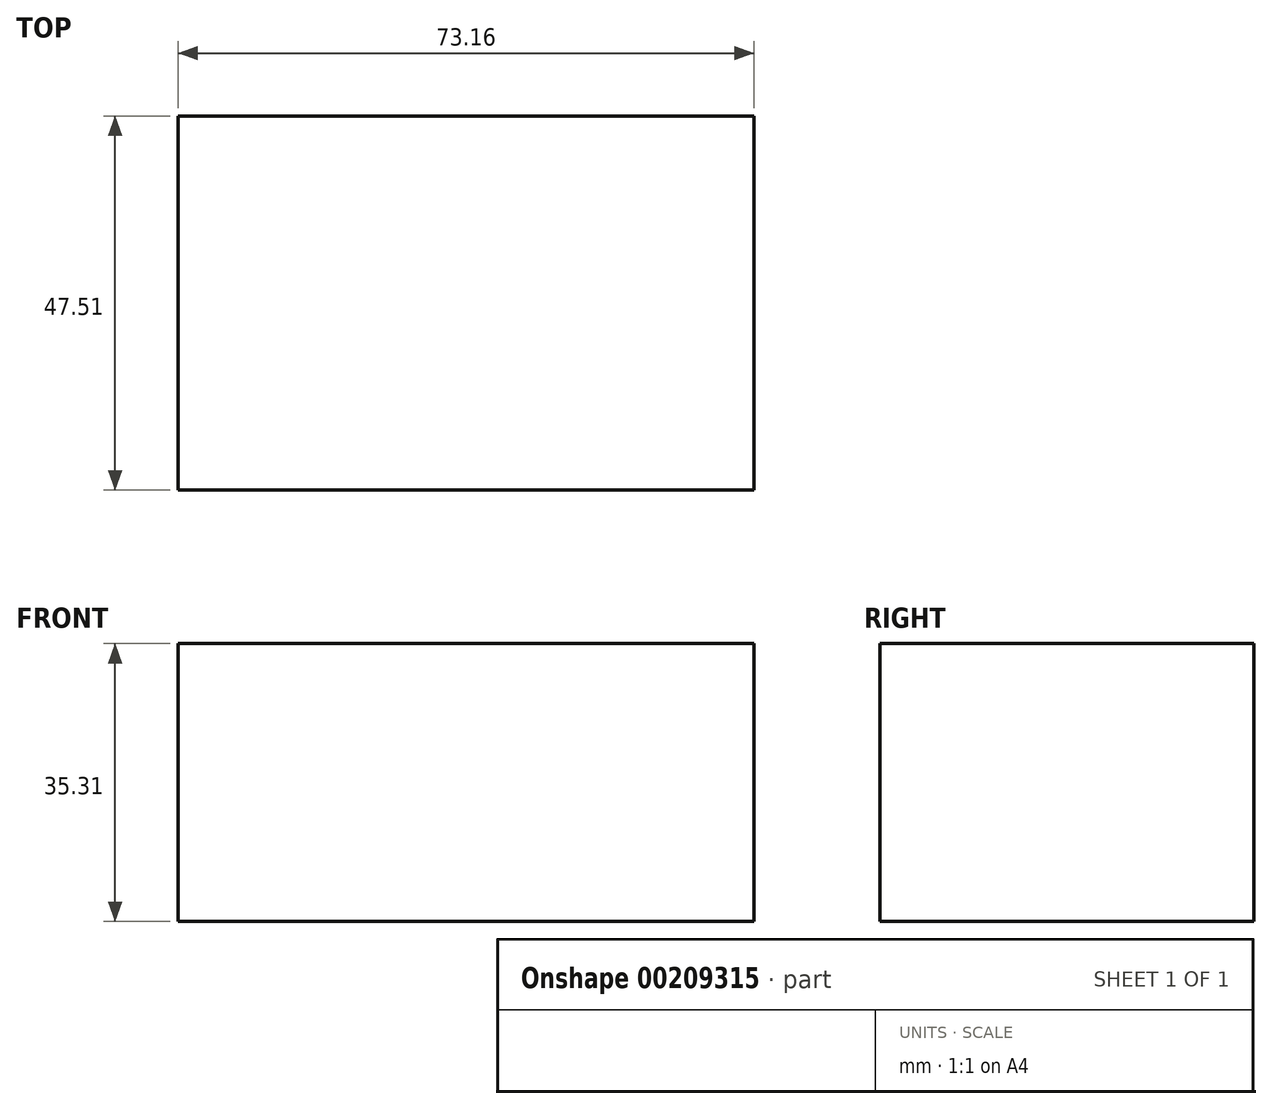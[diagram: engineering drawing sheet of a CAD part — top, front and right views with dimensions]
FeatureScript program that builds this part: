
annotation { "Feature Type Name" : "Feature", "Feature Type Description" : "" }
export const myFeature = defineFeature(function(context is Context, id is Id, definition is map)
    precondition{}
    {
        {
            var Q0;
            Q0=qCreatedBy(makeId("Top.planeOp"),FACE);
            var sketch = newSketch(context, id + "F0", { "sketchPlane" : qUnion([Q0])});
            skLineSegment(sketch, "E0.bottom", {"start": v(-37.6, 22.88) * mm, "end": v(35.56, 22.88) * mm});
            skLineSegment(sketch, "E0.top", {"start": v(-37.6, -24.63) * mm, "end": v(35.56, -24.63) * mm});
            skLineSegment(sketch, "E0.left", {"start": v(-37.6, 22.88) * mm, "end": v(-37.6, -24.63) * mm});
            skLineSegment(sketch, "E0.right", {"start": v(35.56, 22.88) * mm, "end": v(35.56, -24.63) * mm});
            skSolve(sketch);
        }
        {
            var Q0;
            Q0=makeQuery(id+"F0.imprint","IMPRINT",FACE,{"disambiguationData":[TD([[makeQuery(id+"F0.imprint","IMPRINT",EDGE,{"derivedFrom":sQuery(id+"F0.wireOp",EDGE,"E0.bottom")}),-1.0]])]});
            extrude(context, id + "F1", {"entities" : qUnion([Q0]), "depth" : 35.3 * mm});
        }
    });
